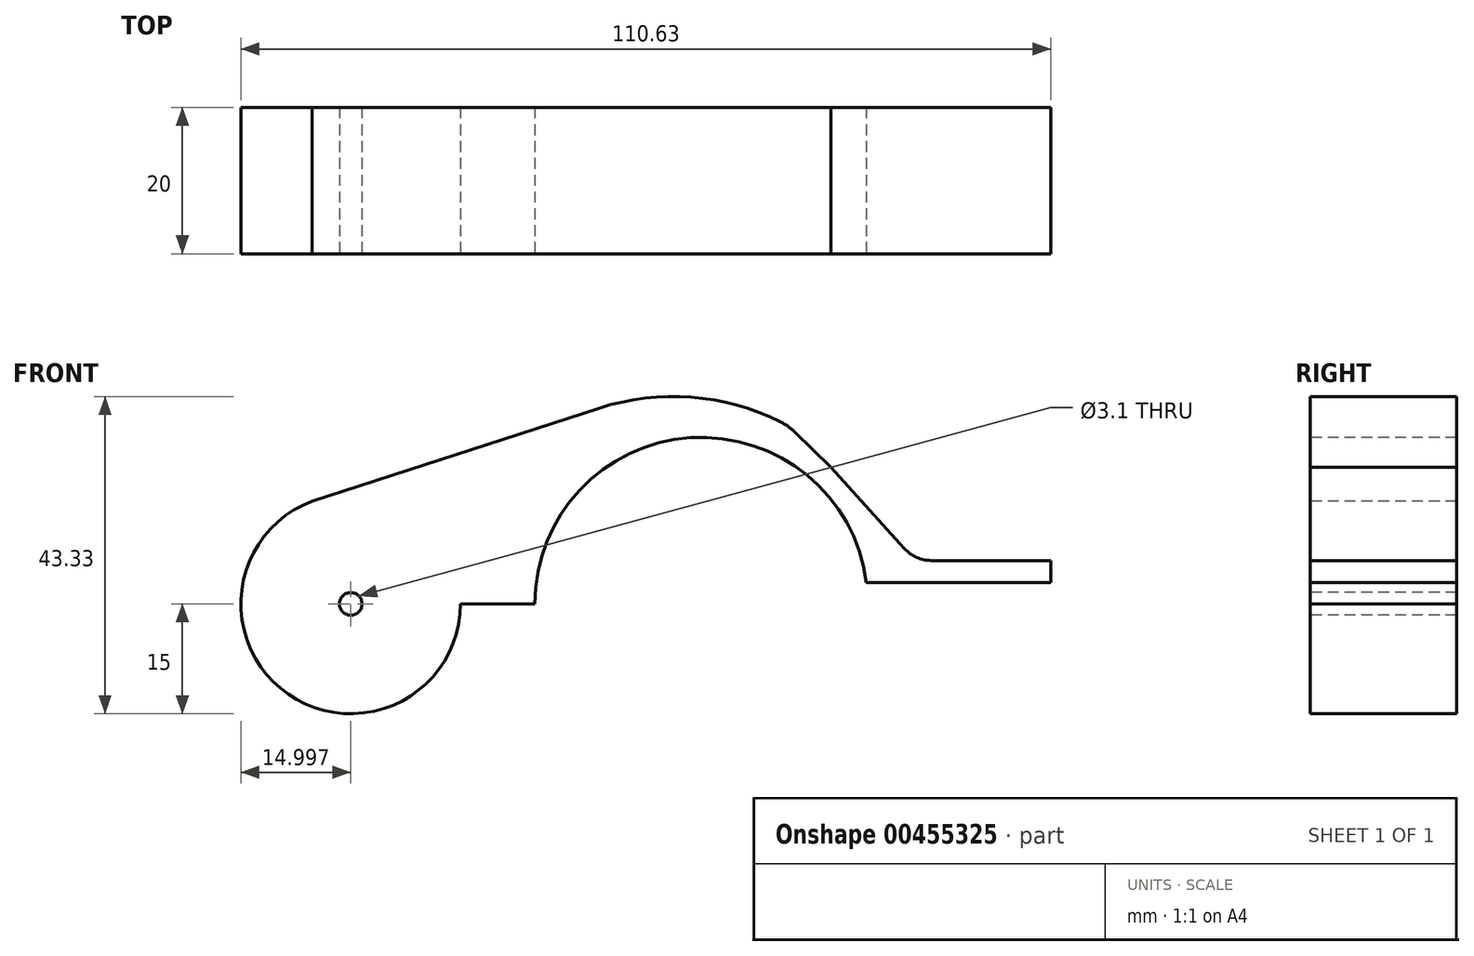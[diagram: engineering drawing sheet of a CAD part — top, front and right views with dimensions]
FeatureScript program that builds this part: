
annotation { "Feature Type Name" : "Feature", "Feature Type Description" : "" }
export const myFeature = defineFeature(function(context is Context, id is Id, definition is map)
    precondition{}
    {
        {
            var Q0;
            Q0=qCreatedBy(makeId("Front.planeOp"),FACE);
            var sketch = newSketch(context, id + "F0", { "sketchPlane" : qUnion([Q0])});
            skArc(sketch, "E0", {"start": v(22.56, 2.93) * mm, "mid": v(-1.47, 22.7) * mm, "end": v(-22.75, 0) * mm});
            skLineSegment(sketch, "E1", {"start": v(25.58, 2.93) * mm, "end": v(47.75, 2.93) * mm});
            skLineSegment(sketch, "E2", {"start": v(47.75, 2.93) * mm, "end": v(47.75, 5.93) * mm});
            skLineSegment(sketch, "E3", {"start": v(47.75, 5.93) * mm, "end": v(31.45, 5.93) * mm});
            skLineSegment(sketch, "E4", {"start": v(12.78, 23.48) * mm, "end": v(17.72, 18.69) * mm});
            skLineSegment(sketch, "E5", {"start": v(27.73, 7.58) * mm, "end": v(17.72, 18.69) * mm});
            skArc(sketch, "E6.filletArc", {"start": v(27.73, 7.58) * mm, "mid": v(29.41, 6.36) * mm, "end": v(31.45, 5.93) * mm});
            skLineSegment(sketch, "E7", {"start": v(25.58, 2.93) * mm, "end": v(22.56, 2.93) * mm});
            skCircle(sketch, "E8", {"center": v(-47.88, 0) * mm, "radius": 15 * mm});
            skLineSegment(sketch, "E9", {"start": v(-13.9, 26.75) * mm, "end": v(-53.16, 14.04) * mm});
            skLineSegment(sketch, "E10", {"start": v(-32.88, 0) * mm, "end": v(-25.75, 0) * mm});
            skCircle(sketch, "E11", {"center": v(-47.88, 0) * mm, "radius": 1.55 * mm});
            skLineSegment(sketch, "E12", {"start": v(-25.75, 0) * mm, "end": v(-22.75, 0) * mm});
            skArc(sketch, "E13", {"start": v(-13.9, 26.75) * mm, "mid": v(-1.37, 28.24) * mm, "end": v(10.78, 24.9) * mm});
            skArc(sketch, "E14.filletArc", {"start": v(12.78, 23.48) * mm, "mid": v(11.83, 24.26) * mm, "end": v(10.78, 24.9) * mm});
            skSolve(sketch);
        }
        {
            var Q0;
            Q0=makeQuery(id+"F0.imprint","IMPRINT",FACE,{"disambiguationData":[TD([[makeQuery(id+"F0.imprint","IMPRINT",EDGE,{"derivedFrom":sQuery(id+"F0.wireOp",EDGE,"E0")}),-1.0]])]});
            var Q1;
            {var subQ0=sQuery(id+"F0.wireOp",EDGE,"E9");var subQ1=sQuery(id+"F0.wireOp",EDGE,"E8");var subQ2=makeQuery(id+"F0.imprint","INTERSECT",VERTEX,{"disambiguationData":[OD(0.0)],"derivedFrom":[subQ1,subQ0]});Q1=makeQuery(id+"F0.imprint","IMPRINT",FACE,{"disambiguationData":[TD([[makeQuery(id+"F0.imprint","IMPRINT",EDGE,{"disambiguationData":[TD([[subQ2,1.0]])],"derivedFrom":subQ1}),1.0]])]});}
            extrude(context, id + "F1", {"entities" : qUnion([Q0, Q1]), "depth" : -20 * mm});
        }
        {
            var Q0;
            Q0=makeQuery(id+"F0.imprint","IMPRINT",FACE,{"disambiguationData":[TD([[makeQuery(id+"F0.imprint","IMPRINT",EDGE,{"derivedFrom":sQuery(id+"F0.wireOp",EDGE,"E11")}),-1.0]])]});
            extrude(context, id + "F2", {"entities" : qUnion([Q0]), "operationType" : NewBodyOperationType.ADD, "depth" : -10 * mm});
        }
    });
